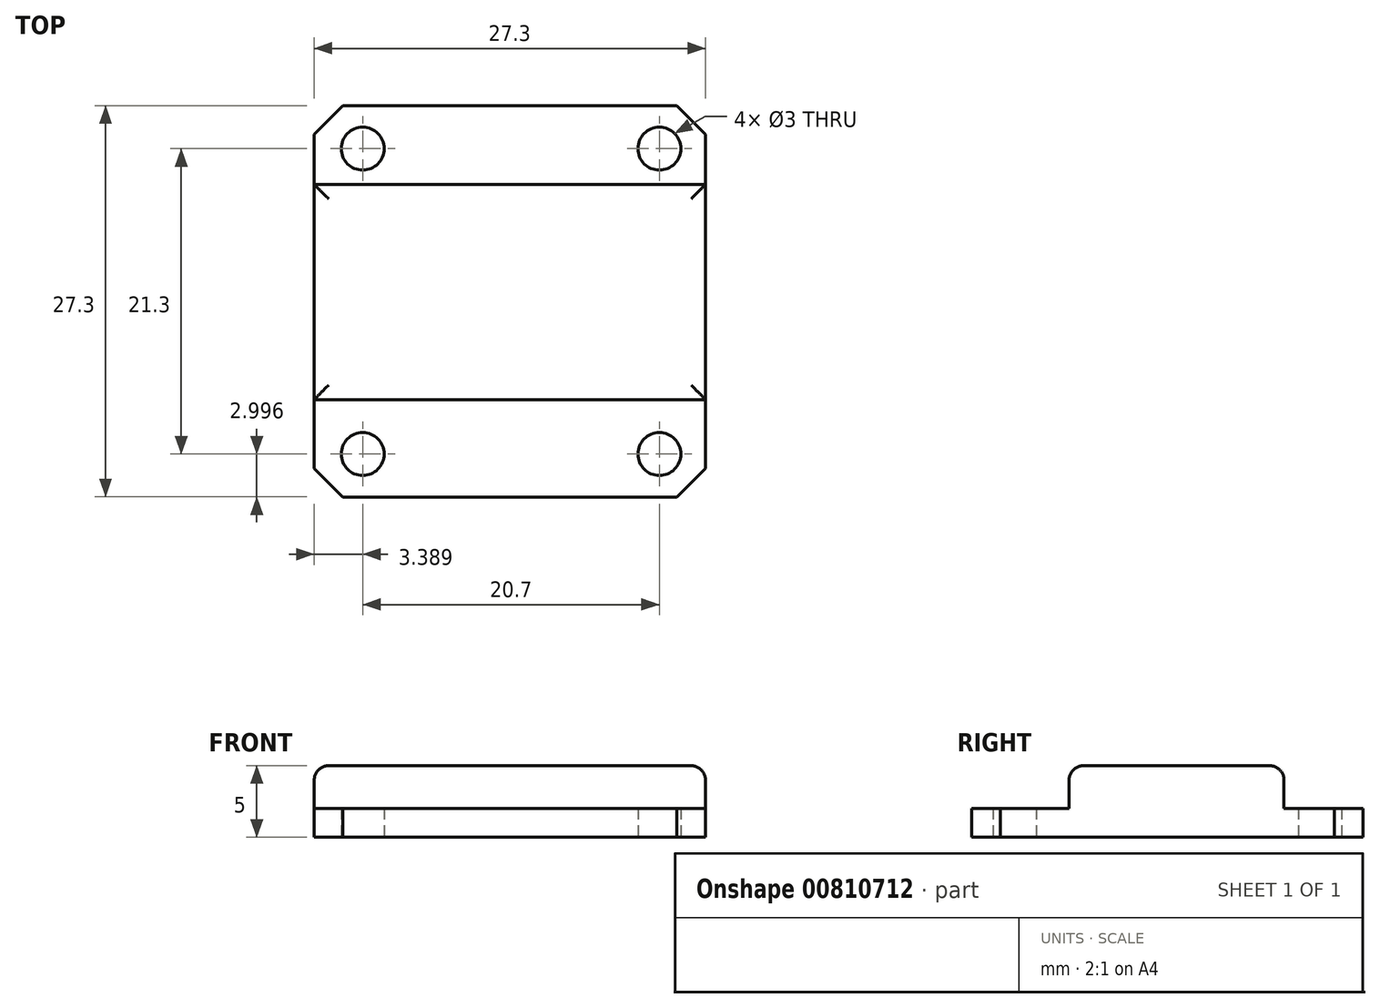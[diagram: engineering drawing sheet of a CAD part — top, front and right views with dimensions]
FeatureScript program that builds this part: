
annotation { "Feature Type Name" : "Feature", "Feature Type Description" : "" }
export const myFeature = defineFeature(function(context is Context, id is Id, definition is map)
    precondition{}
    {
        {
            var Q0;
            Q0=qCreatedBy(makeId("Top.planeOp"),FACE);
            var sketch = newSketch(context, id + "F0", { "sketchPlane" : qUnion([Q0])});
            skLineSegment(sketch, "E0.bottom", {"start": v(-14.28, 15.09) * mm, "end": v(13.02, 15.09) * mm});
            skLineSegment(sketch, "E0.top", {"start": v(-14.28, -12.21) * mm, "end": v(13.02, -12.21) * mm});
            skLineSegment(sketch, "E0.left", {"start": v(-14.28, 15.09) * mm, "end": v(-14.28, -12.21) * mm});
            skLineSegment(sketch, "E0.right", {"start": v(13.02, 15.09) * mm, "end": v(13.02, -12.21) * mm});
            skLineSegment(sketch, "E1", {"start": v(-0.01, 15.09) * mm, "end": v(-0.01, -12.21) * mm, "construction": true});
            skLineSegment(sketch, "E2", {"start": v(-10.9, 15.09) * mm, "end": v(-10.9, -12.21) * mm, "construction": true});
            skLineSegment(sketch, "E3", {"start": v(9.8, 15.09) * mm, "end": v(9.8, -12.21) * mm, "construction": true});
            skCircle(sketch, "E4", {"center": v(-10.9, 12.09) * mm, "radius": 1.5 * mm});
            skCircle(sketch, "E5", {"center": v(9.8, 12.09) * mm, "radius": 1.5 * mm});
            skCircle(sketch, "E6", {"center": v(-10.9, -9.21) * mm, "radius": 1.5 * mm});
            skCircle(sketch, "E7", {"center": v(9.8, -9.21) * mm, "radius": 1.5 * mm});
            skSolve(sketch);
        }
        {
            var Q0;
            Q0=makeQuery(id+"F0.imprint","IMPRINT",FACE,{"disambiguationData":[TD([[makeQuery(id+"F0.imprint","IMPRINT",EDGE,{"derivedFrom":sQuery(id+"F0.wireOp",EDGE,"E0.bottom")}),-1.0]])]});
            extrude(context, id + "F1", {"entities" : qUnion([Q0]), "depth" : 2 * mm, "offsetDistance" : 25 * mm});
        }
        {
            var Q0;
            Q0=makeQuery(id+"F1.opExtrude","SWEPT_EDGE",EDGE,{"disambiguationData":[OSD([sQuery(id+"F0.wireOp",EDGE,"E0.bottom"),sQuery(id+"F0.wireOp",EDGE,"E0.right")])]});
            var Q1;
            Q1=makeQuery(id+"F1.opExtrude","SWEPT_EDGE",EDGE,{"disambiguationData":[OSD([sQuery(id+"F0.wireOp",EDGE,"E0.top"),sQuery(id+"F0.wireOp",EDGE,"E0.right")])]});
            var Q2;
            Q2=makeQuery(id+"F1.opExtrude","SWEPT_EDGE",EDGE,{"disambiguationData":[OSD([sQuery(id+"F0.wireOp",EDGE,"E0.top"),sQuery(id+"F0.wireOp",EDGE,"E0.left")])]});
            var Q3;
            Q3=makeQuery(id+"F1.opExtrude","SWEPT_EDGE",EDGE,{"disambiguationData":[OSD([sQuery(id+"F0.wireOp",EDGE,"E0.bottom"),sQuery(id+"F0.wireOp",EDGE,"E0.left")])]});
            chamfer(context, id + "F2", {"entities" : qUnion([Q0, Q1, Q2, Q3]), "width" : 2 * mm, "tangentPropagation" : true});
        }
        {
            var Q0;
            Q0=makeQuery(id+"F1.opExtrude","CAP_FACE",FACE,{"disambiguationData":[OSD([sQuery(id+"F0.wireOp",EDGE,"E0.bottom"),sQuery(id+"F0.wireOp",EDGE,"E0.top"),sQuery(id+"F0.wireOp",EDGE,"E0.left"),sQuery(id+"F0.wireOp",EDGE,"E0.right"),sQuery(id+"F0.wireOp",EDGE,"E4"),sQuery(id+"F0.wireOp",EDGE,"E5"),sQuery(id+"F0.wireOp",EDGE,"E6"),sQuery(id+"F0.wireOp",EDGE,"E7")])],"isStart":false});
            var sketch = newSketch(context, id + "F3", { "sketchPlane" : qUnion([Q0])});
            skLineSegment(sketch, "E8.bottom", {"start": v(-14.28, 9.58) * mm, "end": v(13.02, 9.58) * mm});
            skLineSegment(sketch, "E8.top", {"start": v(-14.28, -5.42) * mm, "end": v(13.02, -5.42) * mm});
            skLineSegment(sketch, "E8.left", {"start": v(-14.28, 9.58) * mm, "end": v(-14.28, -5.42) * mm});
            skLineSegment(sketch, "E8.right", {"start": v(13.02, 9.58) * mm, "end": v(13.02, -5.42) * mm});
            skSolve(sketch);
        }
        {
            var Q0;
            Q0 = qSketchRegion(id + "F3", true);
            extrude(context, id + "F4", {"entities" : qUnion([Q0]), "operationType" : NewBodyOperationType.ADD, "depth" : 3 * mm, "offsetDistance" : 25 * mm});
        }
        {
            var Q0;
            Q0=makeQuery(id+"F4.opExtrude","CAP_EDGE",EDGE,{"disambiguationData":[OSD([sQuery(id+"F3.wireOp",EDGE,"E8.bottom")])],"isStart":false});
            var Q1;
            Q1=makeQuery(id+"F4.opExtrude","CAP_EDGE",EDGE,{"disambiguationData":[OSD([sQuery(id+"F3.wireOp",EDGE,"E8.top")])],"isStart":false});
            var Q2;
            Q2=makeQuery(id+"F4.opExtrude","CAP_EDGE",EDGE,{"disambiguationData":[OSD([sQuery(id+"F3.wireOp",EDGE,"E8.left")])],"isStart":false});
            var Q3;
            Q3=makeQuery(id+"F4.opExtrude","CAP_EDGE",EDGE,{"disambiguationData":[OSD([sQuery(id+"F3.wireOp",EDGE,"E8.right")])],"isStart":false});
            fillet(context, id + "F5", {"entities" : qUnion([Q0, Q1, Q2, Q3]), "radius" : 1 * mm, "tangentPropagation" : true, "allowEdgeOverflow" : false});
        }
    });
